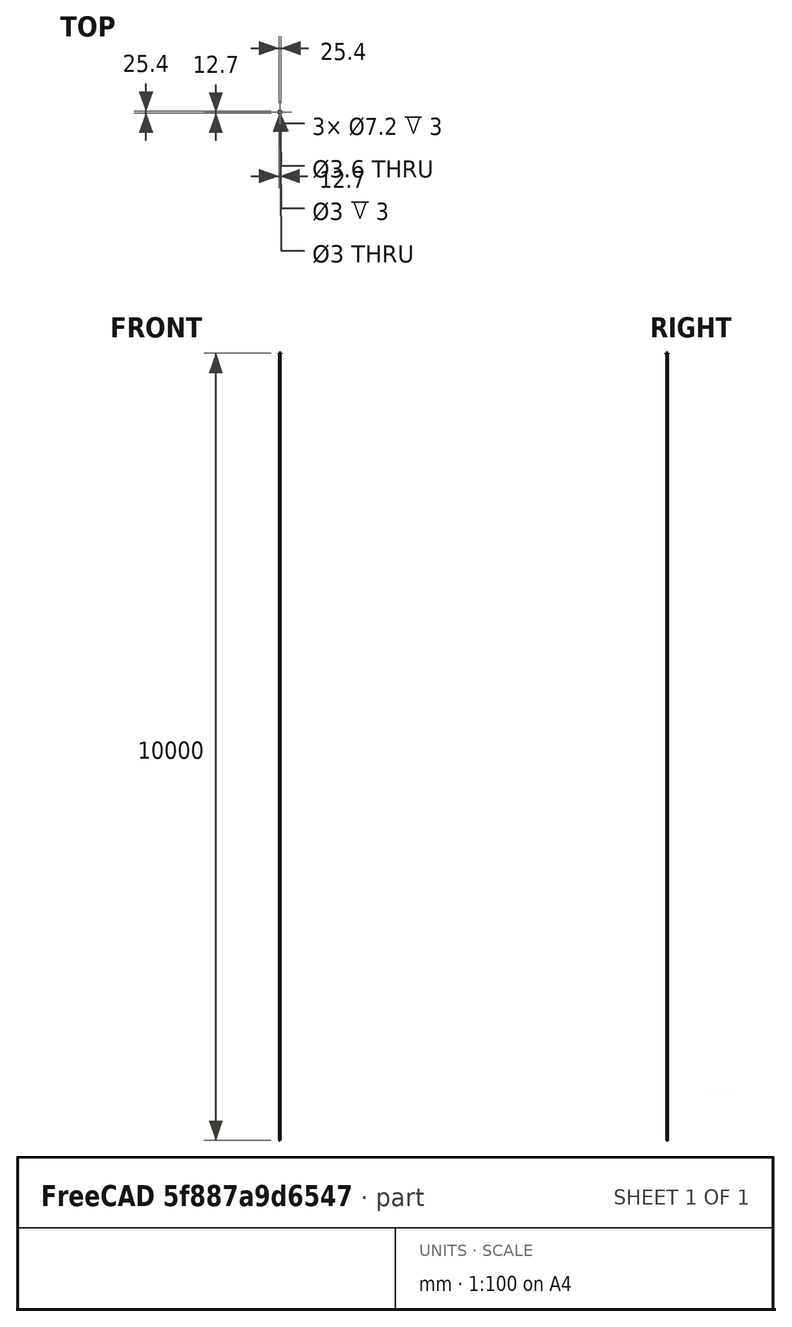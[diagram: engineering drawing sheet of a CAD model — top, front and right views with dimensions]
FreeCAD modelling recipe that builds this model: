
FCSTD DOCUMENT  (FreeCAD 0.15R4671 (Git))
Label: BedFoot
License: All rights reserved
LicenseURL: http://en.wikipedia.org/wiki/All_rights_reserved
objects: Sketcher::SketchObject×6, PartDesign::Pocket×4, PartDesign::Fillet×3, PartDesign::Pad×2, Mesh::Feature×1
note: 21 computed .brp shape members not serialized (recipe doc carries the construction recipe); baked Part::Feature solids carry a one-line shape summary decoded from their .brp

FEATURE [Sketcher::SketchObject] Sketch
  sketch-geometry (4):
    g0: LineSegment StartX=-12.7 StartY=12.7 StartZ=0 EndX=12.7 EndY=12.7 EndZ=0
    g1: LineSegment StartX=12.7 StartY=12.7 StartZ=0 EndX=12.7 EndY=-12.7 EndZ=0
    g2: LineSegment StartX=12.7 StartY=-12.7 StartZ=0 EndX=-12.7 EndY=-12.7 EndZ=0
    g3: LineSegment StartX=-12.7 StartY=-12.7 StartZ=0 EndX=-12.7 EndY=12.7 EndZ=0
  constraints (12):
    c: Coincident(g0,g1)
    c: Coincident(g1,g2)
    c: Coincident(g2,g3)
    c: Coincident(g3,g0)
    c: Horizontal(g0)
    c: Horizontal(g2)
    c: Vertical(g1)
    c: Vertical(g3)
    c: DistanceY(g2,g0) = 25.4
    c: DistanceX(g0,g0) = -25.4
    c: DistanceX(g-1,g2) = -12.7
    c: DistanceY(g-1,g2) = -12.7
FEATURE [PartDesign::Pad] Pad
  Length = 6
  Length2 = 100
  Sketch = -> Sketch
  Type = 0
FEATURE [Sketcher::SketchObject] Sketch001
  Placement = pos=(0,0,6) rot=(0,0,1;0rad)
  Support = -> Pad [Face6]
  sketch-geometry (1):
    g0: Circle CenterX=0 CenterY=0 CenterZ=0 NormalX=0 NormalY=0 NormalZ=1 Radius=1.5
  constraints (1):
    c: Radius(g0) = 1.5
FEATURE [PartDesign::Pocket] Pocket
  Length = 5
  Sketch = -> Sketch001
  Type = 1
FEATURE [Sketcher::SketchObject] Sketch002
  Placement = pos=(0,0,6) rot=(0,0,1;0rad)
  Support = -> Pocket [Face5]
  sketch-geometry (1):
    g0: Circle CenterX=0 CenterY=0 CenterZ=0 NormalX=0 NormalY=0 NormalZ=1 Radius=3.6
  constraints (1):
    c: Radius(g0) = 3.6
FEATURE [PartDesign::Pocket] Pocket001
  Length = 3
  Sketch = -> Sketch002
  Type = 0
FEATURE [PartDesign::Fillet] Fillet
  Base = -> Pocket001 [Edge8,Edge5,Edge2,Edge1]
  Radius = 1
FEATURE [Sketcher::SketchObject] Sketch003
  Placement = pos=(0,0,0) rot=(1,0,0;3.14159rad)
  Support = -> Fillet [Face2]
  sketch-geometry (1):
    g0: Circle CenterX=0 CenterY=0 CenterZ=0 NormalX=0 NormalY=0 NormalZ=1 Radius=5.06197
FEATURE [Mesh::Feature] HexNutStyle1_M3
  Placement = pos=(14.2,22,-121) rot=(0,0,1;0rad)
FEATURE [PartDesign::Pad] Pad001
  Length = 4.5
  Length2 = 100
  Sketch = -> Sketch003
  Type = 0
FEATURE [Sketcher::SketchObject] Sketch004
  Placement = pos=(0,0,-4.5) rot=(1,0,0;3.14159rad)
  Support = -> Pad001 [Face1]
  sketch-geometry (7):
    g0: LineSegment StartX=0 StartY=3.31322 StartZ=0 EndX=-2.86933 EndY=1.65661 EndZ=0
    g1: LineSegment StartX=-2.86933 StartY=1.65661 StartZ=0 EndX=-2.86933 EndY=-1.65661 EndZ=0
    g2: LineSegment StartX=-2.86933 StartY=-1.65661 StartZ=0 EndX=0 EndY=-3.31322 EndZ=0
    g3: LineSegment StartX=0 StartY=-3.31322 StartZ=0 EndX=2.86933 EndY=-1.65661 EndZ=0
    g4: LineSegment StartX=2.86933 StartY=-1.65661 StartZ=0 EndX=2.86933 EndY=1.65661 EndZ=0
    g5: LineSegment StartX=2.86933 StartY=1.65661 StartZ=0 EndX=0 EndY=3.31322 EndZ=0
    g6: Circle [constr] CenterX=0 CenterY=0 CenterZ=0 NormalX=0 NormalY=0 NormalZ=1 Radius=3.31322
  constraints (13):
    c: Coincident(g0,g1)
    c: Coincident(g1,g2)
    c: Coincident(g2,g3)
    c: Coincident(g3,g4)
    c: Coincident(g4,g5)
    c: Coincident(g5,g0)
    c: Equal(g0, g1-g5) x5
    c: PointOnObject(g0,g6)
    c: PointOnObject(g1,g6)
    c: PointOnObject(g2,g6)
    c: PointOnObject(g3,g6)
    c: PointOnObject(g4,g6)
    c: PointOnObject(g5,g6)
FEATURE [PartDesign::Pocket] Pocket002
  Length = 3
  Sketch = -> Sketch004
  Type = 0
FEATURE [Sketcher::SketchObject] Sketch005
  Placement = pos=(0,0,3) rot=(0,0,1;0rad)
  Support = -> Pocket002 [Face21]
  sketch-geometry (1):
    g0: Circle CenterX=0 CenterY=0 CenterZ=0 NormalX=0 NormalY=0 NormalZ=1 Radius=1.8
  constraints (1):
    c: Radius(g0) = 1.8
FEATURE [PartDesign::Pocket] Pocket003
  Length = 5
  Sketch = -> Sketch005
  Type = 1
FEATURE [PartDesign::Fillet] Fillet001
  Base = -> Pocket003 [Edge8,Edge1]
  Radius = 1
FEATURE [PartDesign::Fillet] Fillet002  label="BedFoot"
  Base = -> Fillet001 [Edge35]
  Radius = 3
